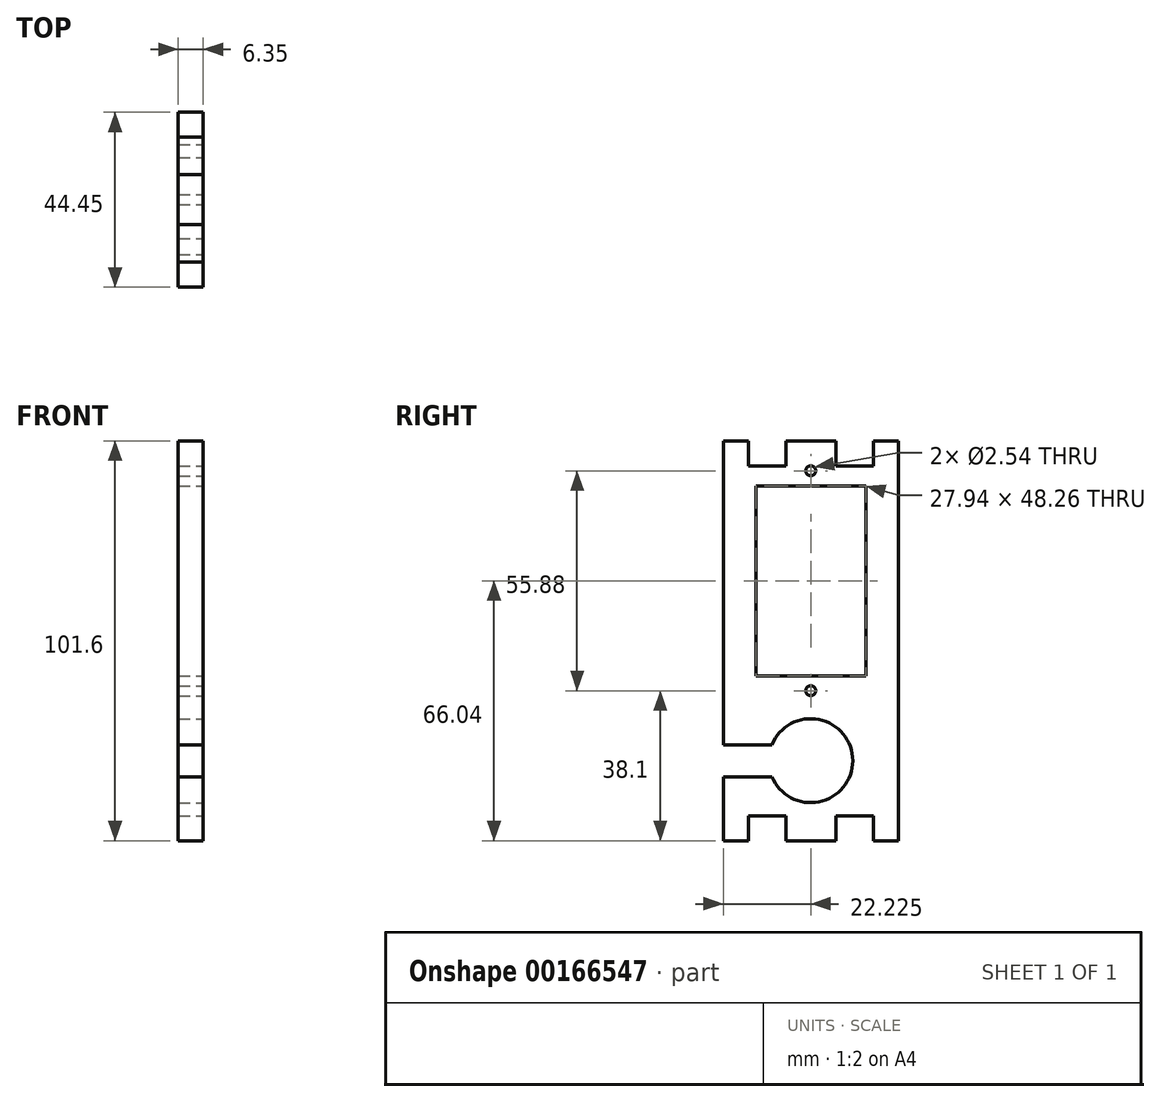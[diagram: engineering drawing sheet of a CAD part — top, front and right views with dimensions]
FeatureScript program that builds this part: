
annotation { "Feature Type Name" : "Feature", "Feature Type Description" : "" }
export const myFeature = defineFeature(function(context is Context, id is Id, definition is map)
    precondition{}
    {
        {
            var Q0;
            Q0=qCreatedBy(makeId("Right.planeOp"),FACE);
            var sketch = newSketch(context, id + "F0", { "sketchPlane" : qUnion([Q0])});
            skLineSegment(sketch, "E0.bottom", {"start": v(0, 0) * mm, "end": v(44.45, 0) * mm});
            skLineSegment(sketch, "E0.top", {"start": v(0, 88.9) * mm, "end": v(44.45, 88.9) * mm});
            skLineSegment(sketch, "E0.left", {"start": v(0, 0) * mm, "end": v(0, 88.9) * mm});
            skLineSegment(sketch, "E0.right", {"start": v(44.45, 0) * mm, "end": v(44.45, 88.9) * mm});
            skSolve(sketch);
        }
        {
            var Q0;
            Q0 = qSketchRegion(id + "F0", true);
            extrude(context, id + "F1", {"entities" : qUnion([Q0]), "depth" : 6.35 * mm});
        }
        {
            var Q0;
            Q0=makeQuery(id+"F1.opExtrude","CAP_FACE",FACE,{"disambiguationData":[OSD([sQuery(id+"F0.wireOp",EDGE,"E0.bottom"),sQuery(id+"F0.wireOp",EDGE,"E0.top"),sQuery(id+"F0.wireOp",EDGE,"E0.left"),sQuery(id+"F0.wireOp",EDGE,"E0.right")])],"isStart":false});
            var sketch = newSketch(context, id + "F2", { "sketchPlane" : qUnion([Q0])});
            skLineSegment(sketch, "E1.bottom", {"start": v(0, 88.9) * mm, "end": v(6.35, 88.9) * mm});
            skLineSegment(sketch, "E1.top", {"start": v(0, 95.25) * mm, "end": v(6.35, 95.25) * mm});
            skLineSegment(sketch, "E1.left", {"start": v(0, 88.9) * mm, "end": v(0, 95.25) * mm});
            skLineSegment(sketch, "E1.right", {"start": v(6.35, 88.9) * mm, "end": v(6.35, 95.25) * mm});
            skLineSegment(sketch, "E2.bottom", {"start": v(0, 0) * mm, "end": v(6.35, 0) * mm});
            skLineSegment(sketch, "E2.top", {"start": v(0, -6.35) * mm, "end": v(6.35, -6.35) * mm});
            skLineSegment(sketch, "E2.left", {"start": v(0, 0) * mm, "end": v(0, -6.35) * mm});
            skLineSegment(sketch, "E2.right", {"start": v(6.35, 0) * mm, "end": v(6.35, -6.35) * mm});
            skLineSegment(sketch, "E3", {"start": v(22.22, 88.9) * mm, "end": v(22.23, 0) * mm, "construction": true});
            skLineSegment(sketch, "E4.MirrorCS", {"start": v(38.1, 88.9) * mm, "end": v(38.1, 95.25) * mm});
            skLineSegment(sketch, "E5.MirrorCS", {"start": v(44.45, 95.25) * mm, "end": v(38.1, 95.25) * mm});
            skLineSegment(sketch, "E6.MirrorCS", {"start": v(44.45, 88.9) * mm, "end": v(44.45, 95.25) * mm});
            skLineSegment(sketch, "E7.MirrorCS", {"start": v(44.45, 88.9) * mm, "end": v(38.1, 88.9) * mm});
            skLineSegment(sketch, "E8.MirrorCS", {"start": v(44.45, 0) * mm, "end": v(38.1, 0) * mm});
            skLineSegment(sketch, "E9.MirrorCS", {"start": v(44.45, 0) * mm, "end": v(44.45, -6.35) * mm});
            skLineSegment(sketch, "E10.MirrorCS", {"start": v(44.45, -6.35) * mm, "end": v(38.1, -6.35) * mm});
            skLineSegment(sketch, "E11.MirrorCS", {"start": v(38.1, 0) * mm, "end": v(38.1, -6.35) * mm});
            skLineSegment(sketch, "E12.bottom", {"start": v(15.87, 88.9) * mm, "end": v(28.57, 88.9) * mm});
            skLineSegment(sketch, "E12.top", {"start": v(15.87, 95.25) * mm, "end": v(28.57, 95.25) * mm});
            skLineSegment(sketch, "E12.left", {"start": v(15.87, 88.9) * mm, "end": v(15.87, 95.25) * mm});
            skLineSegment(sketch, "E12.right", {"start": v(28.57, 88.9) * mm, "end": v(28.57, 95.25) * mm});
            skLineSegment(sketch, "E13.bottom", {"start": v(15.87, 0) * mm, "end": v(28.57, 0) * mm});
            skLineSegment(sketch, "E13.top", {"start": v(15.87, -6.35) * mm, "end": v(28.57, -6.35) * mm});
            skLineSegment(sketch, "E13.left", {"start": v(15.87, 0) * mm, "end": v(15.87, -6.35) * mm});
            skLineSegment(sketch, "E13.right", {"start": v(28.57, 0) * mm, "end": v(28.57, -6.35) * mm});
            skSolve(sketch);
        }
        {
            var Q0;
            Q0 = qSketchRegion(id + "F2", true);
            extrude(context, id + "F3", {"entities" : qUnion([Q0]), "operationType" : NewBodyOperationType.ADD, "oppositeDirection" : true, "depth" : 6.35 * mm});
        }
        {
            var Q0;
            {var subQ0=sQuery(id+"F2.wireOp",EDGE,"E2.right");var subQ1=sQuery(id+"F2.wireOp",EDGE,"E2.left");var subQ2=sQuery(id+"F2.wireOp",EDGE,"E2.top");var subQ3=sQuery(id+"F2.wireOp",EDGE,"E2.bottom");var subQ4=sQuery(id+"F2.wireOp",EDGE,"E1.right");var subQ5=sQuery(id+"F2.wireOp",EDGE,"E1.left");var subQ6=sQuery(id+"F2.wireOp",EDGE,"E1.top");var subQ7=sQuery(id+"F2.wireOp",EDGE,"E1.bottom");Q0=makeQuery(id+"F9rIAaM4ehdyv1n_1.1.F3.boolean.opBoolean","MERGE",FACE,{"derivedFrom":[makeQuery(id+"F3.boolean.opBoolean","MERGE",FACE,{"derivedFrom":[makeQuery(id+"F1.opExtrude","CAP_FACE",FACE,{"disambiguationData":[OSD([sQuery(id+"F0.wireOp",EDGE,"E0.bottom"),sQuery(id+"F0.wireOp",EDGE,"E0.top"),sQuery(id+"F0.wireOp",EDGE,"E0.left"),sQuery(id+"F0.wireOp",EDGE,"E0.right")])],"isStart":false}),makeQuery(id+"F3.opExtrude","CAP_FACE",FACE,{"disambiguationData":[OSD([subQ7,subQ6,subQ5,subQ4])],"isStart":true}),makeQuery(id+"F3.opExtrude","CAP_FACE",FACE,{"disambiguationData":[OSD([subQ3,subQ2,subQ1,subQ0])],"isStart":true})]}),makeQuery(id+"F9rIAaM4ehdyv1n_1.1.F3.opExtrude","CAP_FACE",FACE,{"disambiguationData":[OSD([subQ7,subQ6,subQ5,subQ4])],"isStart":true}),makeQuery(id+"F9rIAaM4ehdyv1n_1.1.F3.opExtrude","CAP_FACE",FACE,{"disambiguationData":[OSD([subQ3,subQ2,subQ1,subQ0])],"isStart":true})]});}
            var sketch = newSketch(context, id + "F4", { "sketchPlane" : qUnion([Q0])});
            skLineSegment(sketch, "E14", {"start": v(22.23, 0) * mm, "end": v(22.23, 88.9) * mm, "construction": true});
            skPoint(sketch, "E15", {"position": v(44.45, 88.9) * mm});
            skPoint(sketch, "E16", {"position": v(0, 88.9) * mm});
            skPoint(sketch, "E17", {"position": v(44.45, 0) * mm});
            skCircle(sketch, "E18", {"center": v(22.23, 13.97) * mm, "radius": 10.67 * mm});
            skLineSegment(sketch, "E19.bottom", {"start": v(8.25, 83.82) * mm, "end": v(36.2, 83.82) * mm});
            skLineSegment(sketch, "E19.top", {"start": v(8.26, 35.56) * mm, "end": v(36.2, 35.56) * mm});
            skLineSegment(sketch, "E19.left", {"start": v(8.25, 83.82) * mm, "end": v(8.25, 35.56) * mm});
            skLineSegment(sketch, "E19.right", {"start": v(36.2, 83.82) * mm, "end": v(36.2, 35.56) * mm});
            skPoint(sketch, "E20", {"position": v(22.22, 83.82) * mm});
            skCircle(sketch, "E21", {"center": v(22.22, 87.63) * mm, "radius": 1.27 * mm});
            skCircle(sketch, "E22", {"center": v(22.23, 31.75) * mm, "radius": 1.27 * mm});
            skPoint(sketch, "E23", {"position": v(22.23, 59.69) * mm});
            skPoint(sketch, "E24", {"position": v(22.23, 35.56) * mm});
            skPoint(sketch, "E25", {"position": v(22.23, 24.64) * mm});
            skSolve(sketch);
        }
        {
            var Q0;
            Q0 = qSketchRegion(id + "F4", true);
            extrude(context, id + "F5", {"entities" : qUnion([Q0]), "operationType" : NewBodyOperationType.REMOVE, "oppositeDirection" : true, "depth" : 25.4 * mm});
        }
        {
            var Q0;
            Q0=makeQuery(id+"F3.boolean.opBoolean","MERGE",FACE,{"derivedFrom":[makeQuery(id+"F1.opExtrude","CAP_FACE",FACE,{"disambiguationData":[OSD([sQuery(id+"F0.wireOp",EDGE,"E0.bottom"),sQuery(id+"F0.wireOp",EDGE,"E0.top"),sQuery(id+"F0.wireOp",EDGE,"E0.left"),sQuery(id+"F0.wireOp",EDGE,"E0.right")])],"isStart":false}),makeQuery(id+"F3.opExtrude","CAP_FACE",FACE,{"disambiguationData":[OSD([sQuery(id+"F2.wireOp",EDGE,"E1.bottom"),sQuery(id+"F2.wireOp",EDGE,"E1.top"),sQuery(id+"F2.wireOp",EDGE,"E1.left"),sQuery(id+"F2.wireOp",EDGE,"E1.right")])],"isStart":true}),makeQuery(id+"F3.opExtrude","CAP_FACE",FACE,{"disambiguationData":[OSD([sQuery(id+"F2.wireOp",EDGE,"E2.bottom"),sQuery(id+"F2.wireOp",EDGE,"E2.top"),sQuery(id+"F2.wireOp",EDGE,"E2.left"),sQuery(id+"F2.wireOp",EDGE,"E2.right")])],"isStart":true}),makeQuery(id+"F3.opExtrude","CAP_FACE",FACE,{"disambiguationData":[OSD([sQuery(id+"F2.wireOp",EDGE,"E4.MirrorCS"),sQuery(id+"F2.wireOp",EDGE,"E5.MirrorCS"),sQuery(id+"F2.wireOp",EDGE,"E6.MirrorCS"),sQuery(id+"F2.wireOp",EDGE,"E7.MirrorCS")])],"isStart":true}),makeQuery(id+"F3.opExtrude","CAP_FACE",FACE,{"disambiguationData":[OSD([sQuery(id+"F2.wireOp",EDGE,"E8.MirrorCS"),sQuery(id+"F2.wireOp",EDGE,"E9.MirrorCS"),sQuery(id+"F2.wireOp",EDGE,"E10.MirrorCS"),sQuery(id+"F2.wireOp",EDGE,"E11.MirrorCS")])],"isStart":true}),makeQuery(id+"F3.opExtrude","CAP_FACE",FACE,{"disambiguationData":[OSD([sQuery(id+"F2.wireOp",EDGE,"E12.bottom"),sQuery(id+"F2.wireOp",EDGE,"E12.top"),sQuery(id+"F2.wireOp",EDGE,"E12.left"),sQuery(id+"F2.wireOp",EDGE,"E12.right")])],"isStart":true}),makeQuery(id+"F3.opExtrude","CAP_FACE",FACE,{"disambiguationData":[OSD([sQuery(id+"F2.wireOp",EDGE,"E13.bottom"),sQuery(id+"F2.wireOp",EDGE,"E13.top"),sQuery(id+"F2.wireOp",EDGE,"E13.left"),sQuery(id+"F2.wireOp",EDGE,"E13.right")])],"isStart":true})]});
            var sketch = newSketch(context, id + "F6", { "sketchPlane" : qUnion([Q0])});
            skLineSegment(sketch, "E26.bottom", {"start": v(12.36, 18.03) * mm, "end": v(0, 18.03) * mm});
            skLineSegment(sketch, "E26.top", {"start": v(12.36, 9.9) * mm, "end": v(0, 9.9) * mm});
            skLineSegment(sketch, "E26.left", {"start": v(12.36, 18.03) * mm, "end": v(12.36, 9.9) * mm});
            skLineSegment(sketch, "E26.right", {"start": v(0, 18.03) * mm, "end": v(0, 9.9) * mm});
            skSolve(sketch);
        }
        {
            var Q0;
            Q0 = qSketchRegion(id + "F6", true);
            extrude(context, id + "F7", {"entities" : qUnion([Q0]), "operationType" : NewBodyOperationType.REMOVE, "oppositeDirection" : true, "depth" : 25.4 * mm});
        }
    });
